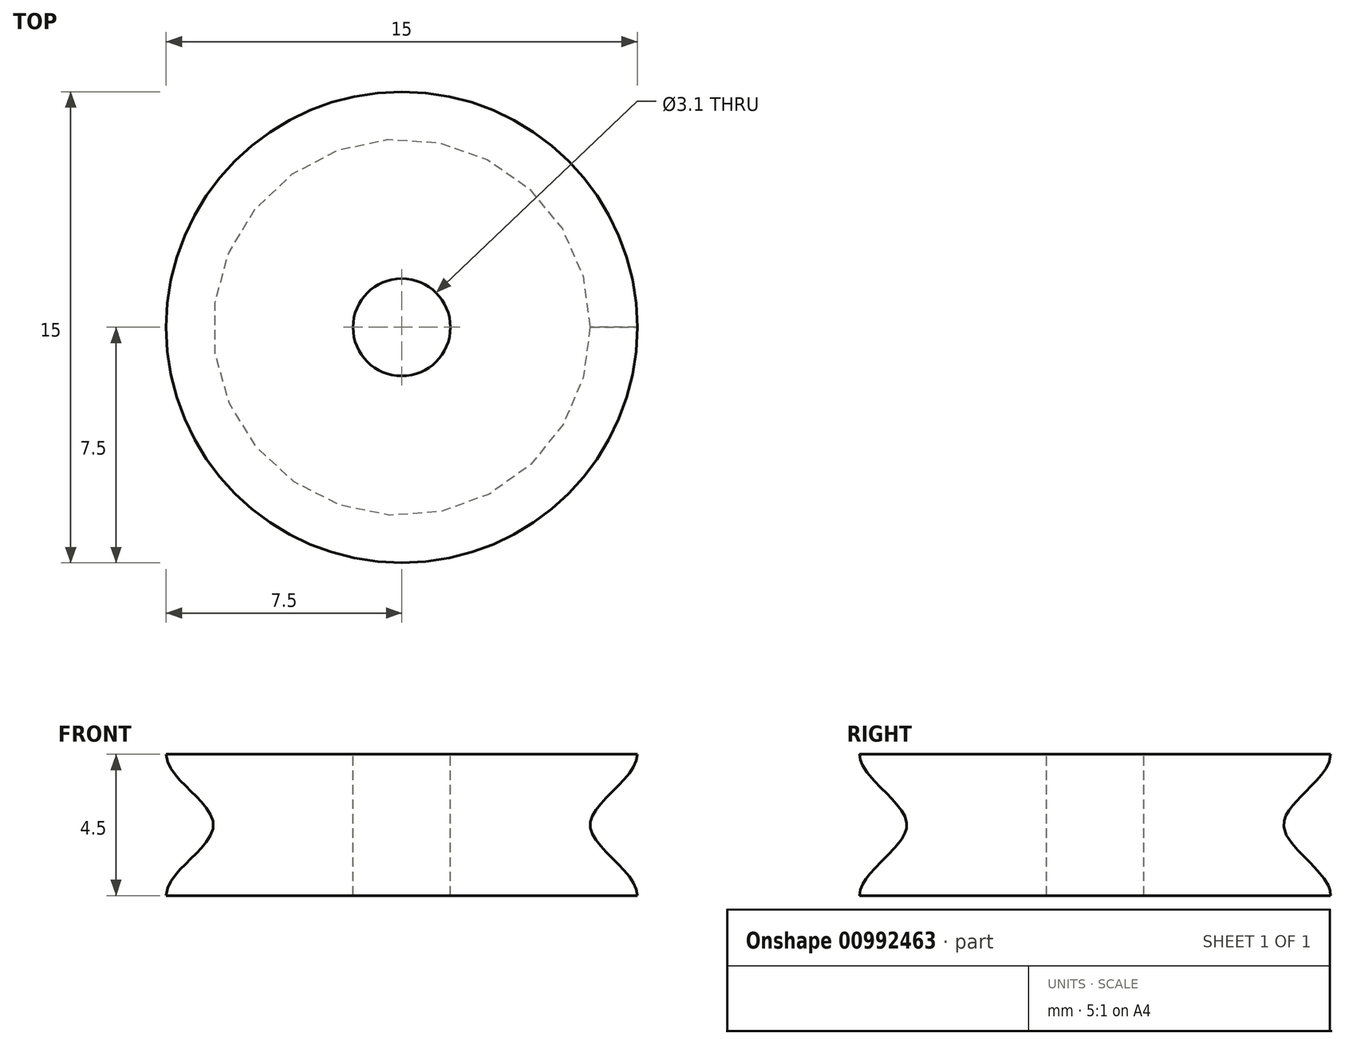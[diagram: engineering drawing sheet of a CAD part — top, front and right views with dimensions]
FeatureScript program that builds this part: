
annotation { "Feature Type Name" : "Feature", "Feature Type Description" : "" }
export const myFeature = defineFeature(function(context is Context, id is Id, definition is map)
    precondition{}
    {
        {
            var Q0;
            Q0=qCreatedBy(makeId("Top.planeOp"),FACE);
            var sketch = newSketch(context, id + "F0", { "sketchPlane" : qUnion([Q0])});
            skCircle(sketch, "E0", {"center": v(0, 0) * mm, "radius": 7.5 * mm});
            skSolve(sketch);
        }
        {
            var Q0;
            Q0=qCreatedBy(makeId("Top.planeOp"),FACE);
            cPlane(context, id + "F1", {"entities" : qUnion([Q0]), "cplaneType" : CPlaneType.OFFSET, "offset" : 2.25 * mm, "width" : 150 * mm, "height" : 150 * mm});
        }
        {
            var Q0;
            Q0=qCreatedBy(id+"F1.planeOp",FACE);
            var sketch = newSketch(context, id + "F2", { "sketchPlane" : qUnion([Q0])});
            skCircle(sketch, "E1", {"center": v(0, 0) * mm, "radius": 6 * mm});
            skSolve(sketch);
        }
        {
            var Q0;
            Q0=qCreatedBy(id+"F1.planeOp",FACE);
            cPlane(context, id + "F3", {"entities" : qUnion([Q0]), "cplaneType" : CPlaneType.OFFSET, "offset" : 2.25 * mm, "width" : 150 * mm, "height" : 150 * mm});
        }
        {
            var Q0;
            Q0=qCreatedBy(id+"F3.planeOp",FACE);
            var sketch = newSketch(context, id + "F4", { "sketchPlane" : qUnion([Q0])});
            skCircle(sketch, "E2", {"center": v(0, 0) * mm, "radius": 7.5 * mm});
            skSolve(sketch);
        }
        {
            var Q0;
            Q0=makeQuery(id+"F0.imprint","IMPRINT",FACE,{"disambiguationData":[TD([[makeQuery(id+"F0.imprint","IMPRINT",EDGE,{"derivedFrom":sQuery(id+"F0.wireOp",EDGE,"E0")}),1.0]])]});
            var Q1;
            Q1=makeQuery(id+"F2.imprint","IMPRINT",FACE,{"disambiguationData":[TD([[makeQuery(id+"F2.imprint","IMPRINT",EDGE,{"derivedFrom":sQuery(id+"F2.wireOp",EDGE,"E1")}),1.0]])]});
            var Q2;
            Q2=makeQuery(id+"F4.imprint","IMPRINT",FACE,{"disambiguationData":[TD([[makeQuery(id+"F4.imprint","IMPRINT",EDGE,{"derivedFrom":sQuery(id+"F4.wireOp",EDGE,"E2")}),1.0]])]});
            loft(context, id + "F5", {"startCondition" : LoftEndDerivativeType.NORMAL_TO_PROFILE, "startMagnitude" : 1, "endCondition" : LoftEndDerivativeType.NORMAL_TO_PROFILE, "endMagnitude" : 1, "sheetProfilesArray" : [{ "sheetProfileEntities" : qUnion([Q0]) }, { "sheetProfileEntities" : qUnion([Q1]) }, { "sheetProfileEntities" : qUnion([Q2]) }]});
        }
        {
            var Q0;
            Q0=qCreatedBy(id+"F3.planeOp",FACE);
            var sketch = newSketch(context, id + "F6", { "sketchPlane" : qUnion([Q0])});
            skCircle(sketch, "E3", {"center": v(0, 0) * mm, "radius": 1.55 * mm});
            skSolve(sketch);
        }
        {
            var Q0;
            Q0=makeQuery(id+"F6.imprint","IMPRINT",FACE,{"disambiguationData":[TD([[makeQuery(id+"F6.imprint","IMPRINT",EDGE,{"derivedFrom":sQuery(id+"F6.wireOp",EDGE,"E3")}),1.0]])]});
            extrude(context, id + "F7", {"entities" : qUnion([Q0]), "operationType" : NewBodyOperationType.REMOVE, "oppositeDirection" : true, "depth" : 25 * mm, "offsetDistance" : 25 * mm});
        }
    });
